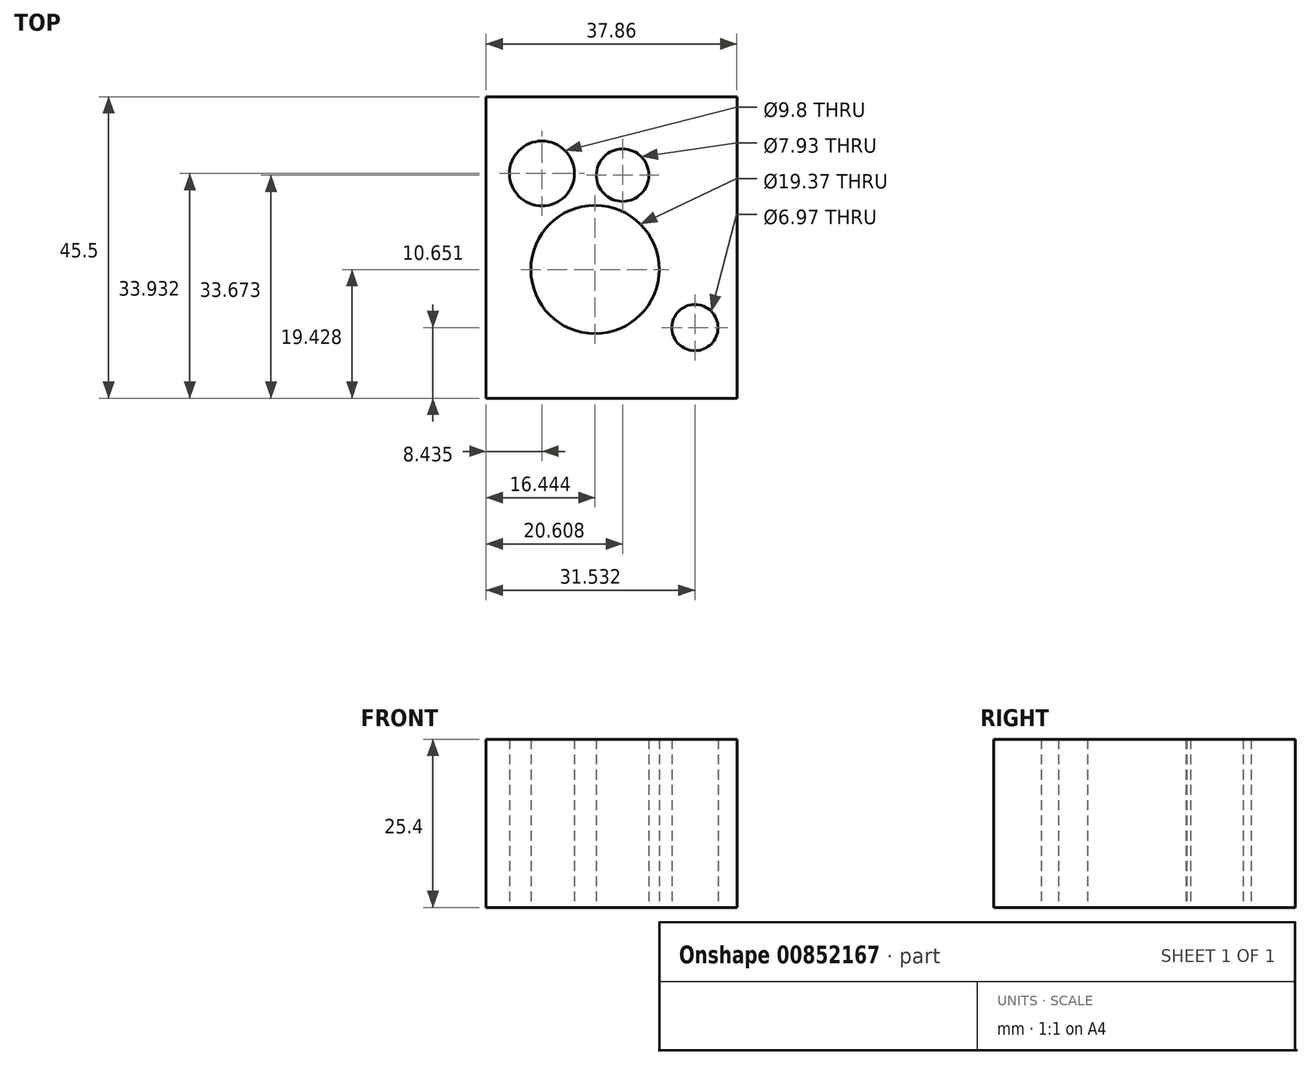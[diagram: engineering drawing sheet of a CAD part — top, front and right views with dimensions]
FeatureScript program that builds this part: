
annotation { "Feature Type Name" : "Feature", "Feature Type Description" : "" }
export const myFeature = defineFeature(function(context is Context, id is Id, definition is map)
    precondition{}
    {
        {
            var Q0;
            Q0=qCreatedBy(makeId("Top.planeOp"),FACE);
            var sketch = newSketch(context, id + "F0", { "sketchPlane" : qUnion([Q0])});
            skLineSegment(sketch, "E0.bottom", {"start": v(0, 0) * mm, "end": v(37.86, 0) * mm});
            skLineSegment(sketch, "E0.top", {"start": v(0, -45.5) * mm, "end": v(37.86, -45.5) * mm});
            skLineSegment(sketch, "E0.left", {"start": v(0, 0) * mm, "end": v(0, -45.5) * mm});
            skLineSegment(sketch, "E0.right", {"start": v(37.86, 0) * mm, "end": v(37.86, -45.5) * mm});
            skCircle(sketch, "E1", {"center": v(8.44, -11.57) * mm, "radius": 4.9 * mm});
            skCircle(sketch, "E2", {"center": v(20.6, -11.83) * mm, "radius": 3.96 * mm});
            skCircle(sketch, "E3", {"center": v(16.44, -26.07) * mm, "radius": 9.69 * mm});
            skCircle(sketch, "E4", {"center": v(31.53, -34.85) * mm, "radius": 3.49 * mm});
            skSolve(sketch);
        }
        {
            var Q0;
            Q0 = qSketchRegion(id + "F0", true);
            extrude(context, id + "F1", {"entities" : qUnion([Q0]), "depth" : 25.4 * mm, "offsetDistance" : 25.4 * mm});
        }
    });
